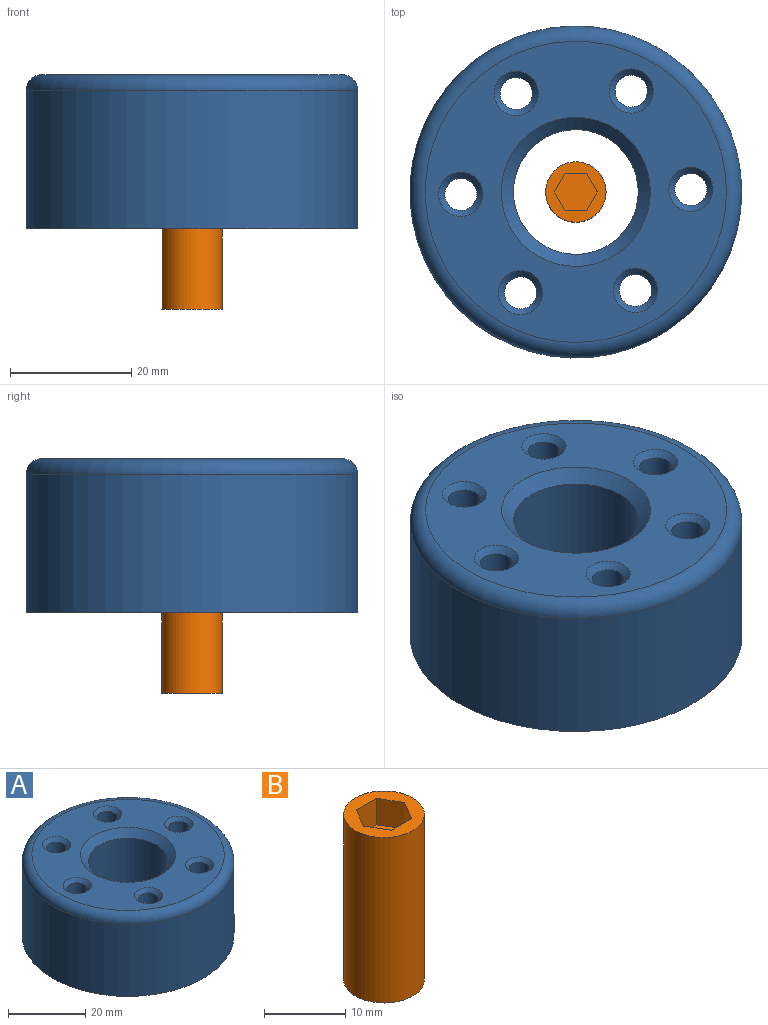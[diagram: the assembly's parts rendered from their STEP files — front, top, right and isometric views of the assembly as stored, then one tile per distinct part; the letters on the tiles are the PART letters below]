
ASSEMBLY  parts=2 mates=1
PART A: 18 faces, bbox 57.3x57.3x25.4 mm
  f0: cylinder r=27.4mm len=54.8mm, axis (0,0,-1), area 3935.7mm2, adj f2,f3
  f1: plane 49.72x49.72mm, normal (0,0,1), area 1215mm2, adj f3,f5,f12,f13,f14,f15,f16,f17
  f2: plane 54.8x54.8mm, normal (0,0,-1), area 1892.8mm2, adj f0,f4,f6,f7,f8,f9,f10,f11
  f3: torus R=24.86mm, axis (0,0,1), area 663.8mm2, adj f0,f1
  f4: cylinder r=10.3mm len=23.4mm, axis (0,0,1), area 1514.8mm2, adj f2,f5
  f5: cone r=10.3mm half-angle=45deg, axis (0,0,1), area 200.9mm2, adj f1,f4
  f6: cylinder r=2.65mm len=24.4mm, axis (0,0,1), area 406.3mm2, adj f2,f13
  f7: cylinder r=2.65mm len=24.4mm, axis (0,0,1), area 406.3mm2, adj f2,f14
  f8: cylinder r=2.65mm len=24.4mm, axis (0,0,1), area 406.3mm2, adj f2,f15
  f9: cylinder r=2.65mm len=24.4mm, axis (0,0,1), area 406.3mm2, adj f2,f16
  f10: cylinder r=2.65mm len=24.4mm, axis (0,0,1), area 406.3mm2, adj f2,f17
  f11: cylinder r=2.65mm len=24.4mm, axis (0,0,1), area 406.3mm2, adj f2,f12
  f12: cone r=2.65mm half-angle=45deg, axis (0,0,1), area 28mm2, adj f1,f11
  f13: cone r=2.65mm half-angle=45deg, axis (0,0,1), area 28mm2, adj f1,f6
  f14: cone r=2.65mm half-angle=45deg, axis (0,0,1), area 28mm2, adj f1,f7
  f15: cone r=2.65mm half-angle=45deg, axis (0,0,1), area 28mm2, adj f1,f8
  f16: cone r=2.65mm half-angle=45deg, axis (0,0,1), area 28mm2, adj f1,f9
  f17: cone r=2.65mm half-angle=45deg, axis (0,0,1), area 28mm2, adj f1,f10
PART B: 10 faces, bbox 10x10x25 mm
  f0: plane 9.96x9.96mm, normal (0,0,1), area 45.3mm2, adj f1,f3,f4,f5,f6,f7,f8
  f1: cylinder r=4.98mm len=25mm, axis (0,0,-1), area 782.6mm2, adj f0,f2
  f2: plane 9.96x9.96mm, normal (0,0,-1), area 78mm2, adj f1
  f3: plane 4x3.55mm, normal (0,-1,0), area 14.2mm2, adj f0,f4,f8,f9
  f4: plane 4x3.07mm, normal (0.87,-0.5,0), area 14.2mm2, adj f0,f3,f5,f9
  f5: plane 4x3.07mm, normal (0.87,0.5,0), area 14.2mm2, adj f0,f4,f6,f9
  f6: plane 4x3.55mm, normal (0,1,0), area 14.2mm2, adj f0,f5,f7,f9
  f7: plane 4x3.07mm, normal (-0.87,0.5,0), area 14.2mm2, adj f0,f6,f8,f9
  f8: plane 4x3.07mm, normal (-0.87,-0.5,0), area 14.2mm2, adj f0,f3,f7,f9
  f9: plane 7.09x6.14mm, normal (0,0,1), area 32.7mm2, adj f3,f4,f5,f6,f7,f8
PLACE A t=(24.77,31.89,14.66)mm
PLACE B t=(-7.26,-12.64,1.36)mm
MATE revolute A.f0 <-> B.f1  axis (0,0,1) through (-61.83,-7.17,26.36)mm
